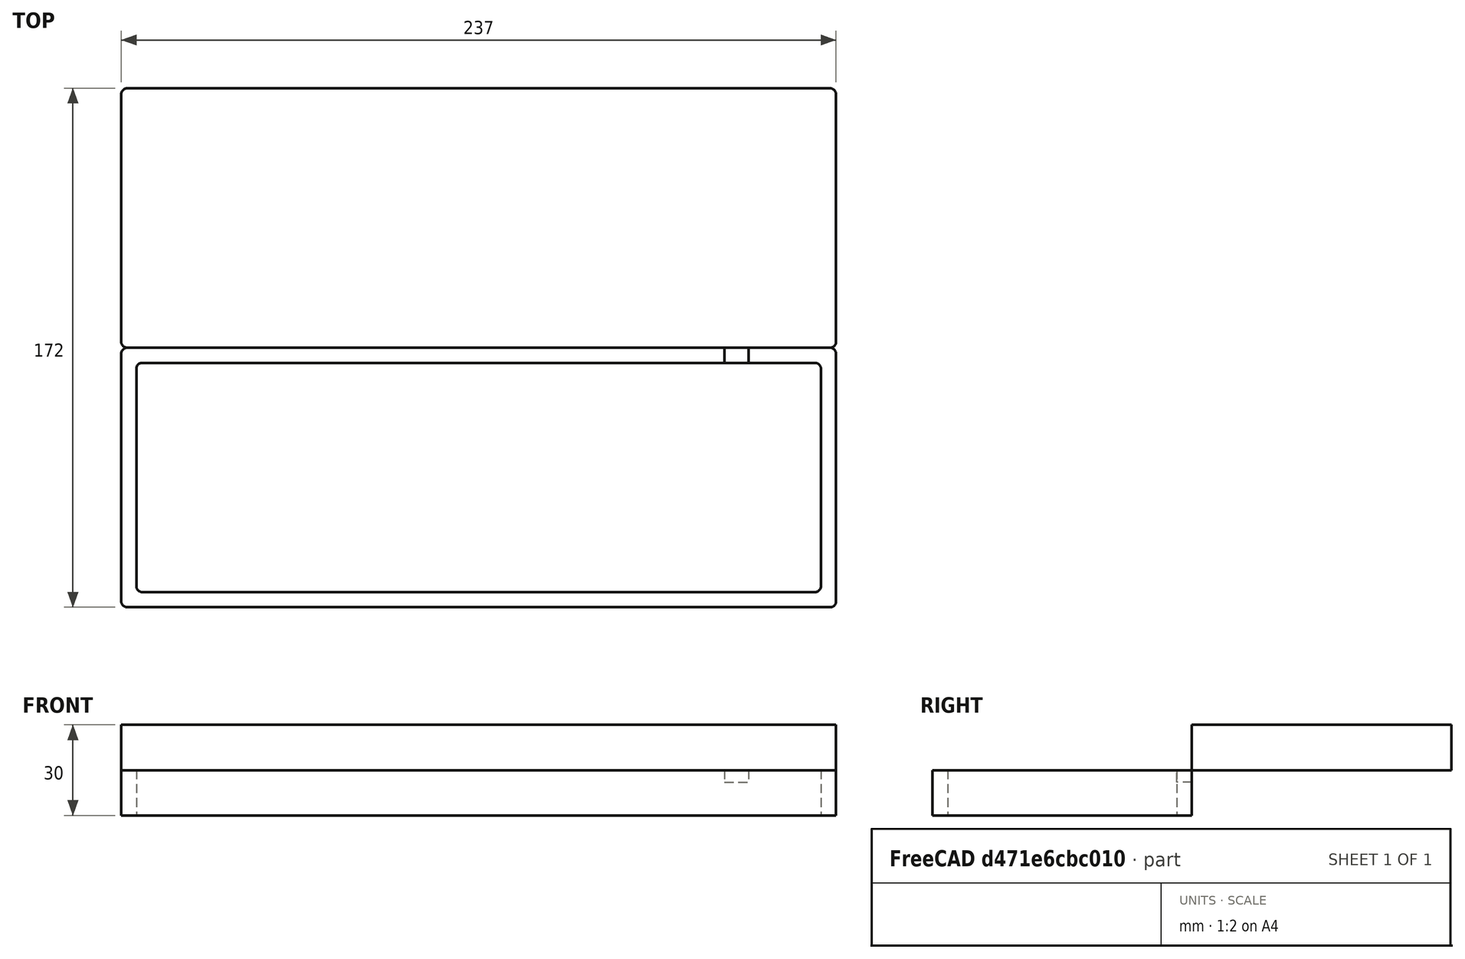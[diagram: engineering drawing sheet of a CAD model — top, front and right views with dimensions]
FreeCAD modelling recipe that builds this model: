
FCSTD DOCUMENT  (FreeCAD 0.16RUnknown)
Label: case_usd
License: All rights reserved
LicenseURL: http://en.wikipedia.org/wiki/All_rights_reserved
objects: App::MeasureDistance×6, Part::Extrusion×3, Part::Part2DObjectPython×2, Part::Cut×2, Part::Box×1
note: 8 computed .brp shape members not serialized (recipe doc carries the construction recipe); baked Part::Feature solids carry a one-line shape summary decoded from their .brp

FEATURE [Part::Part2DObjectPython] Rectangle  # Draft 2D object (typed FeaturePython)
  ChamferSize = 0
  Columns = 1
  FilletRadius = 2
  Height = 76
  Length = 227
  MakeFace = true
  Placement = pos=(5,5,0) rot=(0,0,1;0rad)
  Rows = 1
FEATURE [Part::Part2DObjectPython] Rectangle001  # Draft 2D object (typed FeaturePython)
  ChamferSize = 0
  Columns = 1
  FilletRadius = 2
  Height = 86
  Length = 237
  MakeFace = true
  Rows = 1
FEATURE [Part::Extrusion] Extrude
  Base = -> Rectangle
  Dir = (0,0,15)
  Solid = true
FEATURE [Part::Extrusion] Extrude001
  Base = -> Rectangle001
  Dir = (0,0,15)
  Solid = true
FEATURE [Part::Extrusion] Extrude002
  Base = -> Rectangle001
  Dir = (0,0,15)
  Solid = true
FEATURE [Part::Cut] Cut
  Base = -> Extrude001
  Tool = -> Extrude
FEATURE [Part::Box] Box  label="Cube"
  Height = 4
  Length = 8
  Placement = pos=(200,0,0) rot=(0,0,1;0rad)
  Width = 8
FEATURE [Part::Cut] Cut001
  Base = -> Cut
  Placement = pos=(0,0,0) rot=(1,0,0;3.14159rad)
  Tool = -> Box
FEATURE [App::MeasureDistance] Distance  label="Distance: 86 mm"
  Distance = 86
  P1 = (235,86,15)
  P2 = (234.998,0,15)
FEATURE [App::MeasureDistance] Distance001  label="Distance: 236.995 mm"
  Distance = 236.995
  P1 = (236.995,1.96437,15)
  P2 = (0,2,15)
FEATURE [App::MeasureDistance] Distance002  label="Distance: 5.00026 mm"
  Distance = 5.00026
  P1 = (0,39.7839,15)
  P2 = (5,39.7328,15)
FEATURE [App::MeasureDistance] Distance003  label="Distance: 8.01666 mm"
  Distance = 8.01666
  P1 = (199.997,0,0)
  P2 = (208.014,0,0.00131472)
FEATURE [App::MeasureDistance] Distance004  label="Distance: 3.97675 mm"
  Distance = 3.97675
  P1 = (200,0,3.97675)
  P2 = (200,0,0)
FEATURE [App::MeasureDistance] Distance005  label="Distance: 15 mm"
  Distance = 15
  P1 = (237,83.9635,15)
  P2 = (237,84,0)
